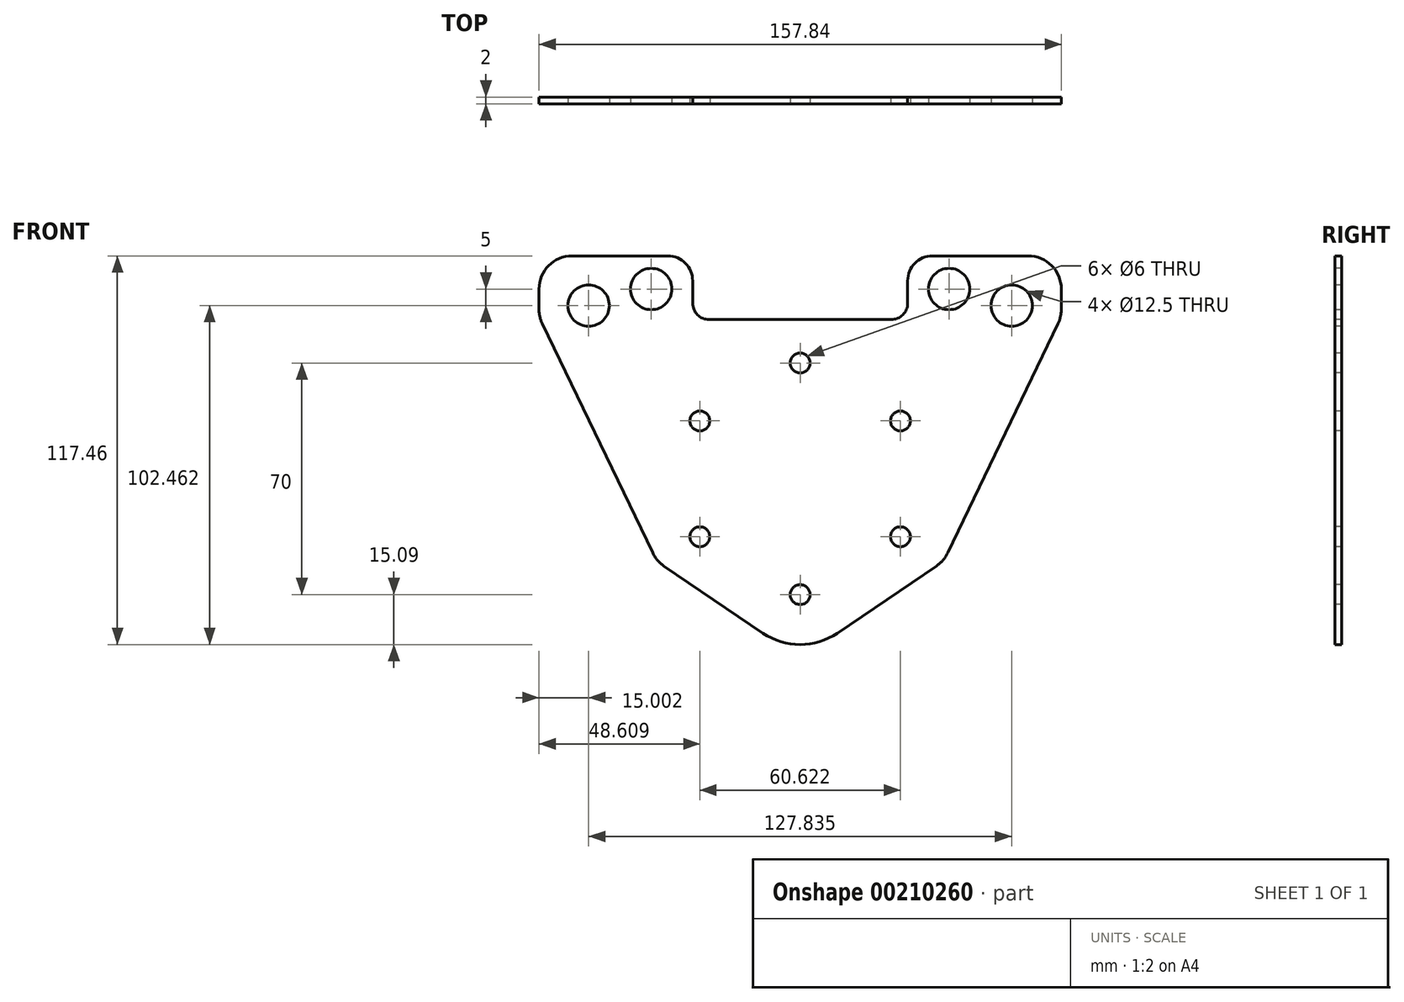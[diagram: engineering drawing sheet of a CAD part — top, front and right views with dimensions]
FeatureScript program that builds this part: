
annotation { "Feature Type Name" : "Feature", "Feature Type Description" : "" }
export const myFeature = defineFeature(function(context is Context, id is Id, definition is map)
    precondition{}
    {
        {
            var Q0;
            Q0=qCreatedBy(makeId("Front.planeOp"),FACE);
            var sketch = newSketch(context, id + "F0", { "sketchPlane" : qUnion([Q0])});
            skCircle(sketch, "E0", {"center": v(0, 0) * mm, "radius": 27.5 * mm});
            skCircle(sketch, "E1", {"center": v(0, 35) * mm, "radius": 3 * mm});
            skCircle(sketch, "E2.1.0", {"center": v(-30.31, 17.5) * mm, "radius": 3 * mm});
            skCircle(sketch, "E2.2.0", {"center": v(-30.31, -17.5) * mm, "radius": 3 * mm});
            skCircle(sketch, "E2.3.0", {"center": v(0, -35) * mm, "radius": 3 * mm});
            skCircle(sketch, "E2.4.0", {"center": v(30.31, -17.5) * mm, "radius": 3 * mm});
            skCircle(sketch, "E2.5.0", {"center": v(30.31, 17.5) * mm, "radius": 3 * mm});
            skLineSegment(sketch, "E3", {"start": v(0, -80) * mm, "end": v(-18, -80) * mm});
            skArc(sketch, "E4", {"start": v(-37.9, -38.47) * mm, "mid": v(-59.22, -23.35) * mm, "end": v(-84, -15) * mm});
            skArc(sketch, "E5", {"start": v(-18, -80) * mm, "mid": v(-25.25, -57.94) * mm, "end": v(-37.9, -38.47) * mm});
            skLineSegment(sketch, "E6", {"start": v(-84, 30) * mm, "end": v(-84, -15) * mm});
            skArc(sketch, "E7", {"start": v(0, 48) * mm, "mid": v(-43.03, 43.8) * mm, "end": v(-84, 30) * mm});
            skArc(sketch, "E8.MirrorCS", {"start": v(0, 48) * mm, "mid": v(43.03, 43.8) * mm, "end": v(84, 30) * mm});
            skLineSegment(sketch, "E9.MirrorCS", {"start": v(84, 30) * mm, "end": v(84, -15) * mm});
            skLineSegment(sketch, "E10.MirrorCS", {"start": v(84, -15) * mm, "end": v(84, -15) * mm});
            skArc(sketch, "E11.MirrorCS", {"start": v(37.9, -38.47) * mm, "mid": v(59.22, -23.35) * mm, "end": v(84, -15) * mm});
            skArc(sketch, "E12.MirrorCS", {"start": v(18, -80) * mm, "mid": v(25.25, -57.94) * mm, "end": v(37.9, -38.47) * mm});
            skLineSegment(sketch, "E13.MirrorCS", {"start": v(0, -80) * mm, "end": v(18, -80) * mm});
            skLineSegment(sketch, "E14", {"start": v(0, 0) * mm, "end": v(37.9, -38.47) * mm});
            skSolve(sketch);
        }
        {
            var Q0;
            Q0=qCreatedBy(makeId("Front.planeOp"),FACE);
            var sketch = newSketch(context, id + "F1", { "sketchPlane" : qUnion([Q0])});
            skCircle(sketch, "E15", {"center": v(-63.92, 52.37) * mm, "radius": 6.25 * mm});
            skCircle(sketch, "E16.MirrorC", {"center": v(63.92, 52.37) * mm, "radius": 6.25 * mm});
            skPoint(sketch, "E17.center", {"position": v(0, 0) * mm});
            skPoint(sketch, "E18.visualSharp", {"position": v(0, -54.25) * mm});
            skArc(sketch, "E18.filletArc", {"start": v(-11.23, -46.64) * mm, "mid": v(0, -50.09) * mm, "end": v(11.23, -46.64) * mm});
            skPoint(sketch, "E19.visualSharp", {"position": v(-80, 0) * mm});
            skPoint(sketch, "E20.visualSharp", {"position": v(80, 0) * mm});
            skCircle(sketch, "E21", {"center": v(-45, 57.37) * mm, "radius": 6.25 * mm});
            skCircle(sketch, "E22.MirrorC", {"center": v(45, 57.37) * mm, "radius": 6.25 * mm});
            skLineSegment(sketch, "E23", {"start": v(-44.59, -22.38) * mm, "end": v(-77.93, 46.9) * mm});
            skLineSegment(sketch, "E24", {"start": v(-11.23, -46.64) * mm, "end": v(-41.19, -26.32) * mm});
            skLineSegment(sketch, "E25.MirrorCS", {"start": v(11.23, -46.64) * mm, "end": v(41.19, -26.32) * mm});
            skLineSegment(sketch, "E26", {"start": v(-68.92, 67.37) * mm, "end": v(-39.99, 67.37) * mm});
            skLineSegment(sketch, "E27", {"start": v(-78.92, 51.23) * mm, "end": v(-78.92, 57.37) * mm});
            skArc(sketch, "E28.filletArc", {"start": v(-68.92, 67.37) * mm, "mid": v(-75.99, 64.44) * mm, "end": v(-78.92, 57.37) * mm});
            skArc(sketch, "E29.filletArc", {"start": v(-78.92, 51.23) * mm, "mid": v(-78.67, 49) * mm, "end": v(-77.93, 46.9) * mm});
            skArc(sketch, "E30.MirrorCS", {"start": v(68.92, 67.37) * mm, "mid": v(75.99, 64.44) * mm, "end": v(78.92, 57.37) * mm});
            skLineSegment(sketch, "E31.MirrorCS", {"start": v(78.92, 51.23) * mm, "end": v(78.92, 57.37) * mm});
            skArc(sketch, "E32.MirrorCS", {"start": v(78.92, 51.23) * mm, "mid": v(78.67, 49) * mm, "end": v(77.93, 46.9) * mm});
            skLineSegment(sketch, "E33.MirrorCS", {"start": v(44.59, -22.38) * mm, "end": v(77.93, 46.9) * mm});
            skLineSegment(sketch, "E34", {"start": v(0, 48.13) * mm, "end": v(-27.49, 48.13) * mm});
            skLineSegment(sketch, "E35", {"start": v(-32.49, 53.13) * mm, "end": v(-32.49, 59.87) * mm});
            skPoint(sketch, "E36.visualSharp", {"position": v(-32.49, 48.13) * mm});
            skArc(sketch, "E36.filletArc", {"start": v(-32.49, 53.13) * mm, "mid": v(-31.02, 49.6) * mm, "end": v(-27.49, 48.13) * mm});
            skPoint(sketch, "E37.visualSharp", {"position": v(-32.49, 67.37) * mm});
            skArc(sketch, "E37.filletArc", {"start": v(-32.49, 59.87) * mm, "mid": v(-34.68, 65.18) * mm, "end": v(-39.99, 67.37) * mm});
            skLineSegment(sketch, "E38.MirrorCS", {"start": v(0, 48.13) * mm, "end": v(27.49, 48.13) * mm});
            skArc(sketch, "E39.MirrorCS", {"start": v(32.49, 53.13) * mm, "mid": v(31.02, 49.6) * mm, "end": v(27.49, 48.13) * mm});
            skLineSegment(sketch, "E40.MirrorCS", {"start": v(32.49, 53.13) * mm, "end": v(32.49, 59.87) * mm});
            skArc(sketch, "E41.MirrorCS", {"start": v(32.49, 59.87) * mm, "mid": v(34.68, 65.18) * mm, "end": v(39.99, 67.37) * mm});
            skLineSegment(sketch, "E42.MirrorCS", {"start": v(68.92, 67.37) * mm, "end": v(39.99, 67.37) * mm});
            skLineSegment(sketch, "E43", {"start": v(0, 0) * mm, "end": v(0, 35) * mm});
            skCircle(sketch, "E44", {"center": v(0, 35) * mm, "radius": 3 * mm});
            skCircle(sketch, "E45.1.0", {"center": v(-30.31, 17.5) * mm, "radius": 3 * mm});
            skCircle(sketch, "E45.2.0", {"center": v(-30.31, -17.5) * mm, "radius": 3 * mm});
            skCircle(sketch, "E45.3.0", {"center": v(0, -35) * mm, "radius": 3 * mm});
            skCircle(sketch, "E45.4.0", {"center": v(30.31, -17.5) * mm, "radius": 3 * mm});
            skCircle(sketch, "E45.5.0", {"center": v(30.31, 17.5) * mm, "radius": 3 * mm});
            skPoint(sketch, "E46.visualSharp", {"position": v(-43.42, -24.8) * mm});
            skArc(sketch, "E46.filletArc", {"start": v(-44.59, -22.38) * mm, "mid": v(-43.15, -24.57) * mm, "end": v(-41.19, -26.32) * mm});
            skPoint(sketch, "E47.visualSharp", {"position": v(43.42, -24.8) * mm});
            skArc(sketch, "E47.filletArc", {"start": v(41.19, -26.32) * mm, "mid": v(43.15, -24.57) * mm, "end": v(44.59, -22.38) * mm});
            skSolve(sketch);
        }
        {
            var Q0;
            Q0=makeQuery(id+"F1.imprint","IMPRINT",FACE,{"disambiguationData":[TD([[makeQuery(id+"F1.imprint","IMPRINT",EDGE,{"derivedFrom":sQuery(id+"F1.wireOp",EDGE,"E15")}),-1.0]])]});
            extrude(context, id + "F2", {"entities" : qUnion([Q0]), "oppositeDirection" : true, "depth" : 2 * mm});
        }
    });
